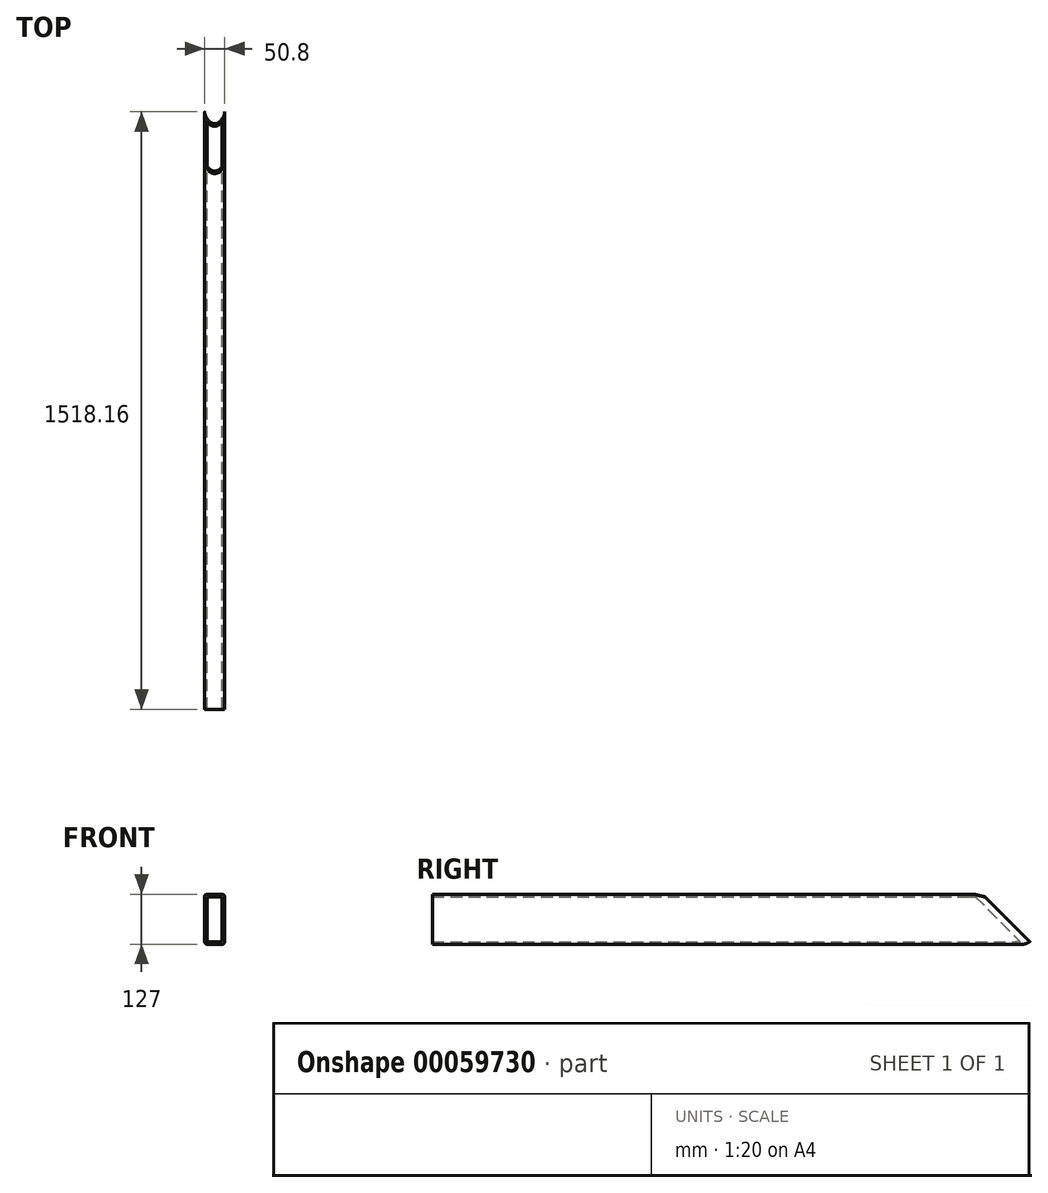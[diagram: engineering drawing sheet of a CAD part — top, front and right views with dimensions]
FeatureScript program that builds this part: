
annotation { "Feature Type Name" : "Feature", "Feature Type Description" : "" }
export const myFeature = defineFeature(function(context is Context, id is Id, definition is map)
    precondition{}
    {
        {
            var Q0;
            Q0=qCreatedBy(makeId("Front.planeOp"),FACE);
            var sketch = newSketch(context, id + "F0", { "sketchPlane" : qUnion([Q0])});
            skLineSegment(sketch, "E0", {"start": v(0, 54.68) * mm, "end": v(0, -53.79) * mm, "construction": true});
            skLineSegment(sketch, "E1", {"start": v(41.42, 0) * mm, "end": v(-38.44, 0) * mm, "construction": true});
            skLineSegment(sketch, "E2.rect.bottom", {"start": v(-19.05, 63.5) * mm, "end": v(17.78, 63.5) * mm});
            skLineSegment(sketch, "E2.rect.top", {"start": v(-19.05, -63.5) * mm, "end": v(19.05, -63.5) * mm});
            skLineSegment(sketch, "E2.rect.left", {"start": v(-25.4, 57.15) * mm, "end": v(-25.4, -57.15) * mm});
            skLineSegment(sketch, "E2.rect.right", {"start": v(25.4, 55.88) * mm, "end": v(25.4, -57.15) * mm});
            skPoint(sketch, "E2.rect.middle", {"position": v(0, 0) * mm});
            skPoint(sketch, "E3.visualSharp", {"position": v(-25.4, 63.5) * mm});
            skArc(sketch, "E3.filletArc", {"start": v(-19.05, 63.5) * mm, "mid": v(-23.54, 61.64) * mm, "end": v(-25.4, 57.15) * mm});
            skPoint(sketch, "E4.visualSharp", {"position": v(25.4, 63.5) * mm});
            skArc(sketch, "E4.filletArc", {"start": v(25.4, 55.88) * mm, "mid": v(23.17, 61.27) * mm, "end": v(17.78, 63.5) * mm});
            skPoint(sketch, "E5.visualSharp", {"position": v(25.4, -63.5) * mm});
            skArc(sketch, "E5.filletArc", {"start": v(19.05, -63.5) * mm, "mid": v(23.54, -61.64) * mm, "end": v(25.4, -57.15) * mm});
            skPoint(sketch, "E6.visualSharp", {"position": v(-25.4, -63.5) * mm});
            skArc(sketch, "E6.filletArc", {"start": v(-25.4, -57.15) * mm, "mid": v(-23.54, -61.64) * mm, "end": v(-19.05, -63.5) * mm});
            skLineSegment(sketch, "E7.0", {"start": v(-19.05, 57.15) * mm, "end": v(-19.05, 57.15) * mm});
            skLineSegment(sketch, "E7.1", {"start": v(-19.05, 57.15) * mm, "end": v(-19.05, -57.15) * mm});
            skLineSegment(sketch, "E7.2", {"start": v(-19.05, 57.15) * mm, "end": v(17.78, 57.15) * mm});
            skLineSegment(sketch, "E7.3", {"start": v(-19.05, -57.15) * mm, "end": v(-19.05, -57.15) * mm});
            skArc(sketch, "E7.4", {"start": v(19.05, 55.88) * mm, "mid": v(18.68, 56.78) * mm, "end": v(17.78, 57.15) * mm});
            skLineSegment(sketch, "E7.5", {"start": v(19.05, 55.88) * mm, "end": v(19.05, -57.15) * mm});
            skLineSegment(sketch, "E7.6", {"start": v(19.05, -57.15) * mm, "end": v(19.05, -57.15) * mm});
            skLineSegment(sketch, "E7.7", {"start": v(-19.05, -57.15) * mm, "end": v(19.05, -57.15) * mm});
            skLineSegment(sketch, "E8", {"start": v(55.43, -63.5) * mm, "end": v(-63.47, -63.5) * mm, "construction": true});
            skSolve(sketch);
        }
        {
            var Q0;
            Q0=makeQuery(id+"F0.imprint","IMPRINT",FACE,{"disambiguationData":[TD([[makeQuery(id+"F0.imprint","IMPRINT",EDGE,{"derivedFrom":sQuery(id+"F0.wireOp",EDGE,"E2.rect.bottom")}),-1.0]])]});
            extrude(context, id + "F1", {"entities" : qUnion([Q0]), "depth" : 1524 * mm});
        }
        {
            var Q0;
            Q0=makeQuery(id+"F1.opExtrude","CAP_EDGE",EDGE,{"disambiguationData":[OSD([sQuery(id+"F0.wireOp",EDGE,"E2.rect.top")])],"isStart":true});
            cPlane(context, id + "F2", {"entities" : qUnion([Q0]), "cplaneType" : CPlaneType.LINE_ANGLE, "offset" : 152.4 * mm, "angle" : 135 * degree, "width" : 152.4 * mm, "height" : 152.4 * mm});
        }
        {
            var Q0;
            Q0=qCreatedBy(id+"F2.planeOp",FACE);
            var sketch = newSketch(context, id + "F3", { "sketchPlane" : qUnion([Q0])});
            skArc(sketch, "E9", {"start": v(-25.4, -44.67) * mm, "mid": v(0, -70.43) * mm, "end": v(25.4, -44.67) * mm});
            skLineSegment(sketch, "E10.bottom", {"start": v(-63.17, -44.67) * mm, "end": v(-25.4, -44.67) * mm});
            skLineSegment(sketch, "E10.top", {"start": v(-63.17, 59.9) * mm, "end": v(58.1, 59.9) * mm});
            skLineSegment(sketch, "E10.left", {"start": v(-63.17, -44.67) * mm, "end": v(-63.17, 59.9) * mm});
            skLineSegment(sketch, "E10.right", {"start": v(58.1, -44.67) * mm, "end": v(58.1, 59.9) * mm});
            skLineSegment(sketch, "E11.trimOffspring", {"start": v(25.4, -44.67) * mm, "end": v(58.1, -44.67) * mm});
            skSolve(sketch);
        }
        {
            var Q0;
            Q0=makeQuery(id+"F3.imprint","IMPRINT",FACE,{"disambiguationData":[TD([[makeQuery(id+"F3.imprint","IMPRINT",EDGE,{"derivedFrom":sQuery(id+"F3.wireOp",EDGE,"E9")}),1.0]])]});
            var Q1;
            Q1=makeQuery(id+"F1.opExtrude","SWEPT_FACE",FACE,{"disambiguationData":[OSD([sQuery(id+"F0.wireOp",EDGE,"E2.rect.bottom")])]});
            extrude(context, id + "F4", {"entities" : qUnion([Q0]), "operationType" : NewBodyOperationType.REMOVE, "endBound" : BoundingType.UP_TO_SURFACE, "endBoundEntityFace" : qUnion([Q1]), "depth" : 25.4 * mm});
        }
    });
